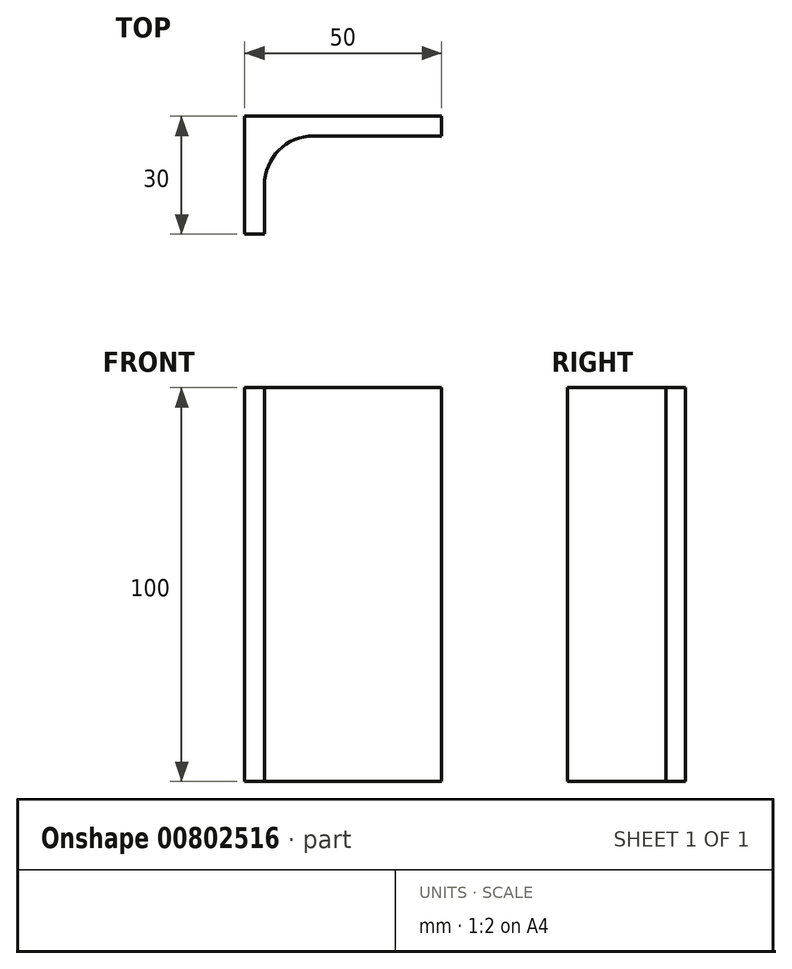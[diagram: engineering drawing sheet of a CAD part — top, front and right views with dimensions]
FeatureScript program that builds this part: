
annotation { "Feature Type Name" : "Feature", "Feature Type Description" : "" }
export const myFeature = defineFeature(function(context is Context, id is Id, definition is map)
    precondition{}
    {
        {
            var Q0;
            Q0=qCreatedBy(makeId("Top.planeOp"),FACE);
            var sketch = newSketch(context, id + "F0", { "sketchPlane" : qUnion([Q0])});
            skLineSegment(sketch, "E0.bottom", {"start": v(0, 0) * mm, "end": v(5, 0) * mm});
            skLineSegment(sketch, "E0.top", {"start": v(0, -25) * mm, "end": v(5, -25) * mm});
            skLineSegment(sketch, "E0.left", {"start": v(0, 0) * mm, "end": v(0, -25) * mm});
            skLineSegment(sketch, "E0.right", {"start": v(5, 0) * mm, "end": v(5, -25) * mm});
            skLineSegment(sketch, "E1.bottom", {"start": v(0, 0) * mm, "end": v(50, 0) * mm});
            skLineSegment(sketch, "E1.top", {"start": v(0, 5) * mm, "end": v(50, 5) * mm});
            skLineSegment(sketch, "E1.left", {"start": v(0, 0) * mm, "end": v(0, 5) * mm});
            skLineSegment(sketch, "E1.right", {"start": v(50, 0) * mm, "end": v(50, 5) * mm});
            skCircle(sketch, "E2", {"center": v(17.5, -12.5) * mm, "radius": 12.5 * mm});
            skPoint(sketch, "E2.first.point", {"position": v(5, -12.5) * mm});
            skPoint(sketch, "E2.second.point", {"position": v(17.5, 0) * mm});
            skPoint(sketch, "E2.third.point", {"position": v(26.41, -3.74) * mm});
            skSolve(sketch);
        }
        {
            var Q0;
            {var subQ1=sQuery(id+"F0.wireOp",EDGE,"E0.top");Q0=makeQuery(id+"F0.imprint","IMPRINT",FACE,{"disambiguationData":[TD([[makeQuery(id+"F0.imprint","IMPRINT",EDGE,{"derivedFrom":subQ1}),1.0]])]});}
            var Q1;
            Q1=makeQuery(id+"F0.imprint","IMPRINT",FACE,{"disambiguationData":[TD([[makeQuery(id+"F0.imprint","IMPRINT",EDGE,{"derivedFrom":sQuery(id+"F0.wireOp",EDGE,"E1.top")}),-1.0]])]});
            var Q2;
            {var subQ0=sQuery(id+"F0.wireOp",EDGE,"E1.bottom");var subQ1=sQuery(id+"F0.wireOp",EDGE,"E0.right");var subQ2=makeQuery(id+"F0.imprint","INTERSECT",VERTEX,{"derivedFrom":[subQ1,subQ0]});Q2=makeQuery(id+"F0.imprint","IMPRINT",FACE,{"disambiguationData":[TD([[makeQuery(id+"F0.imprint","IMPRINT",EDGE,{"disambiguationData":[TD([[subQ2,-1.0]])],"derivedFrom":subQ1}),1.0]])]});}
            extrude(context, id + "F1", {"entities" : qUnion([Q0, Q1, Q2]), "depth" : 100 * mm, "offsetDistance" : 25.4 * mm});
        }
    });
